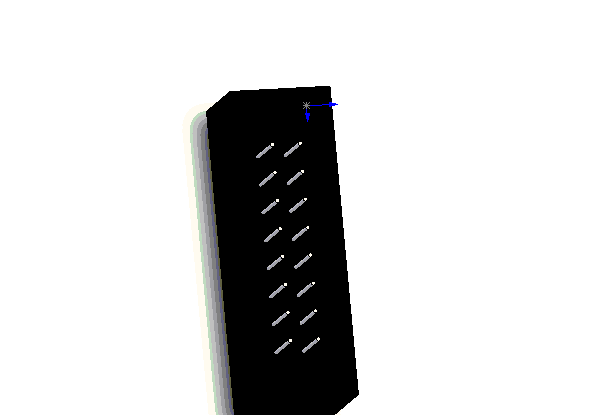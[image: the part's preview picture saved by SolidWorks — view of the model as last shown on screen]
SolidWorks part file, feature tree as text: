
SOLIDWORKS PART (.sldprt)
format: sldprt  version: not decoded by parser v0  size: 158,720 bytes
history: native  units: mm
features: sketch x3, extrude x2, material x1, cut_extrude x1 (+13 scaffold rows collapsed)
feature tree (20):
  scaffold x13  (default folders/planes/origin — collapsed)
  material  "Material <not specified>"
  sketch  "Sketch1"  dims[D1=27.94mm D2=9.144mm]
  extrude  "Extrude1"  Depth=9.779mm
  sketch  "Sketch2"  dims[D1=1.143mm D2=1.143mm D3=1.143mm D4=1.143mm]
  cut_extrude  "Cut-Extrude1"  Depth=5.588mm
  sketch  "Sketch4"  dims[D1=0.381mm D2=3.302mm D3=3.937mm D4=90.0deg D5=3.9878mm]
  extrude  "Extrude3"  Depth=6.096mm
decode coverage: 6 of 6 modeling features carry decoded parameters
note: suppression state not decoded; provenance and decode notes live in map.json
